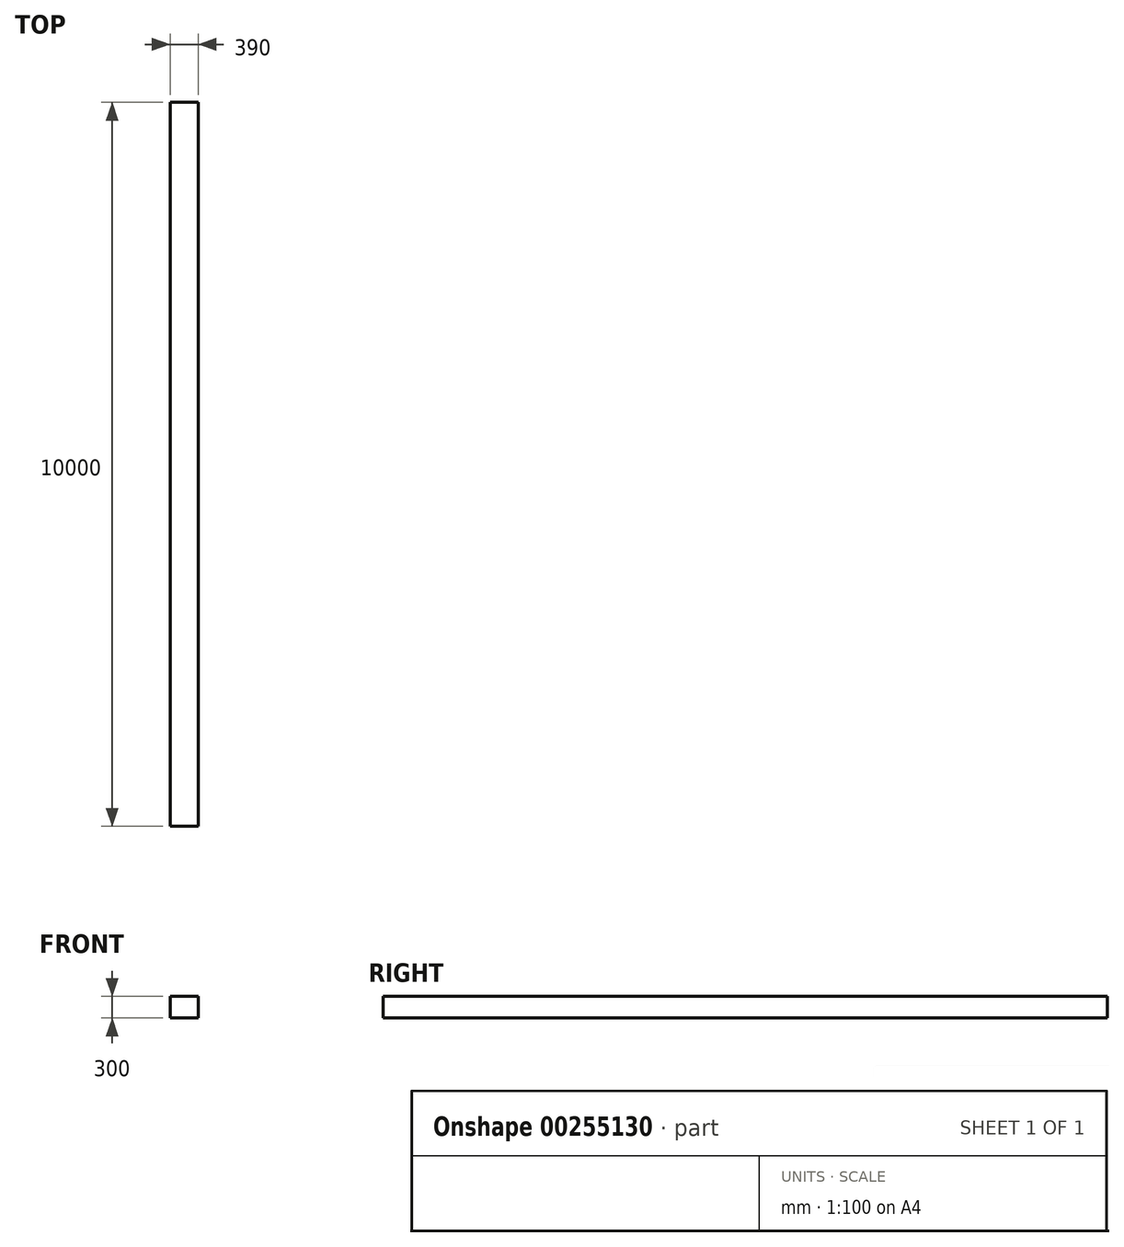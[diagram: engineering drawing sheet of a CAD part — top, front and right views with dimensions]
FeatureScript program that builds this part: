
annotation { "Feature Type Name" : "Feature", "Feature Type Description" : "" }
export const myFeature = defineFeature(function(context is Context, id is Id, definition is map)
    precondition{}
    {
        {
            var Q0;
            Q0=qCreatedBy(makeId("Front.planeOp"),FACE);
            var sketch = newSketch(context, id + "F0", { "sketchPlane" : qUnion([Q0])});
            skLineSegment(sketch, "E0.bottom", {"start": v(195, -150) * mm, "end": v(-195, -150) * mm});
            skLineSegment(sketch, "E0.top", {"start": v(195, 150) * mm, "end": v(-195, 150) * mm});
            skLineSegment(sketch, "E0.left", {"start": v(195, -150) * mm, "end": v(195, 150) * mm});
            skLineSegment(sketch, "E0.right", {"start": v(-195, -150) * mm, "end": v(-195, 150) * mm});
            skPoint(sketch, "E0.middle", {"position": v(0, 0) * mm});
            skSolve(sketch);
        }
        {
            var Q0;
            Q0=makeQuery(id+"F0.imprint","IMPRINT",FACE,{"disambiguationData":[TD([[makeQuery(id+"F0.imprint","IMPRINT",EDGE,{"derivedFrom":sQuery(id+"F0.wireOp",EDGE,"E0.bottom")}),-1.0]])]});
            extrude(context, id + "F1", {"entities" : qUnion([Q0]), "depth" : 10000 * mm});
        }
    });
